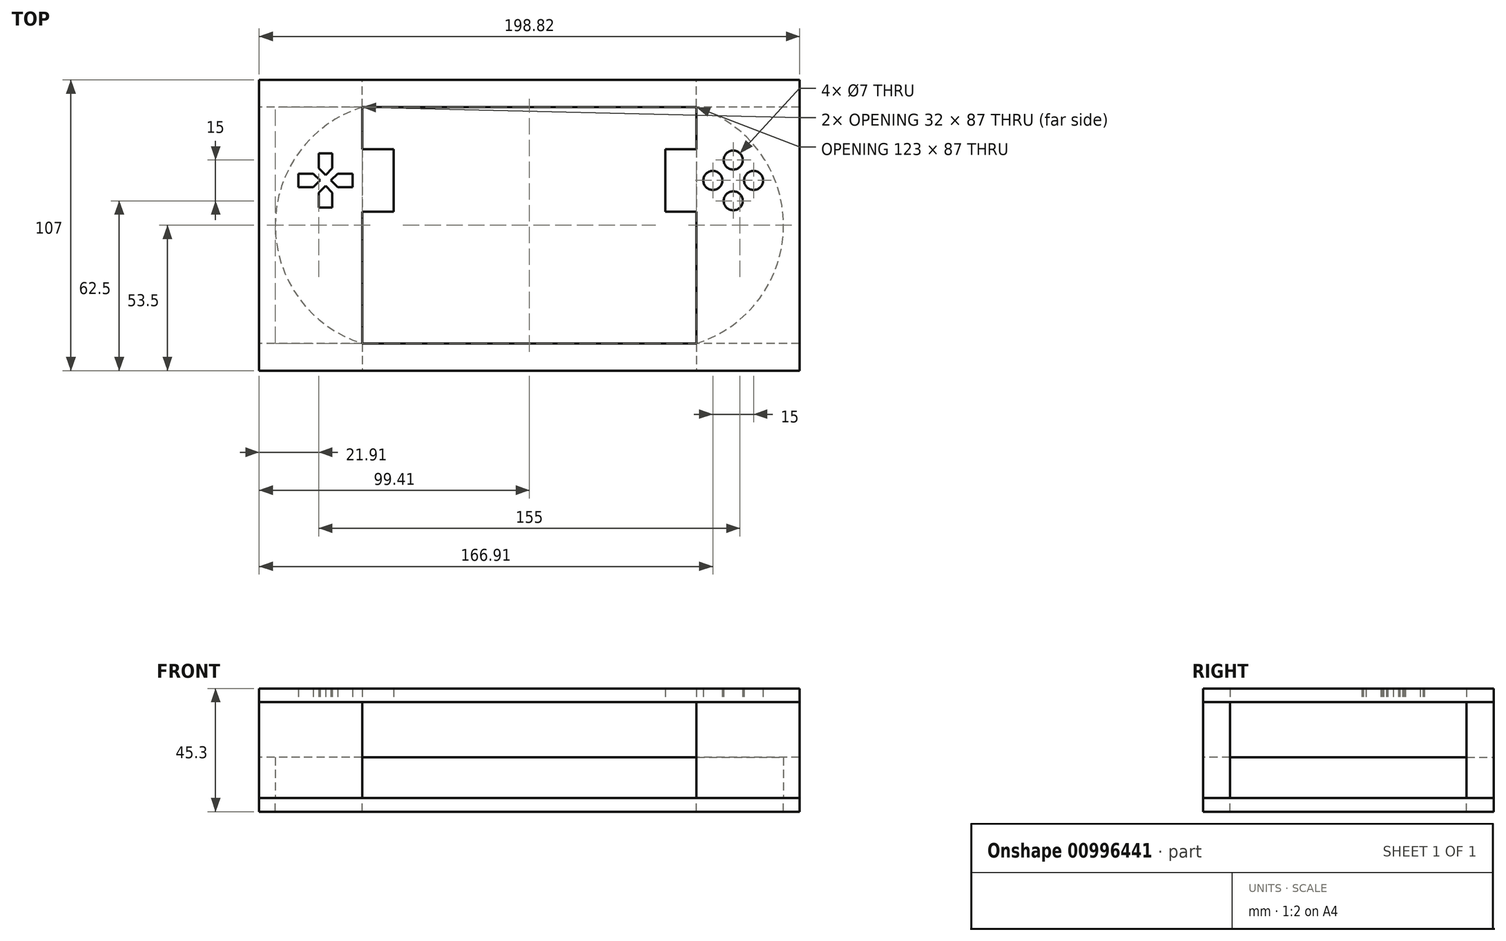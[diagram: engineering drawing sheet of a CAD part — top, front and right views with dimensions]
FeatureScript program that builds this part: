
annotation { "Feature Type Name" : "Feature", "Feature Type Description" : "" }
export const myFeature = defineFeature(function(context is Context, id is Id, definition is map)
    precondition{}
    {
        {
            var Q0;
            Q0=qCreatedBy(makeId("Top.planeOp"),FACE);
            var sketch = newSketch(context, id + "F0", { "sketchPlane" : qUnion([Q0])});
            skLineSegment(sketch, "E0.bottom", {"start": v(61.5, 43.5) * mm, "end": v(-61.5, 43.5) * mm});
            skLineSegment(sketch, "E0.top", {"start": v(61.5, -43.5) * mm, "end": v(-61.5, -43.5) * mm});
            skLineSegment(sketch, "E0.left", {"start": v(61.5, 43.5) * mm, "end": v(61.5, -43.5) * mm});
            skLineSegment(sketch, "E0.right", {"start": v(-61.5, 43.5) * mm, "end": v(-61.5, -43.5) * mm});
            skPoint(sketch, "E0.middle", {"position": v(0, 0) * mm});
            skArc(sketch, "E1", {"start": v(-61.5, 43.5) * mm, "mid": v(-93.5, 0) * mm, "end": v(-61.5, -43.5) * mm});
            skArc(sketch, "E2", {"start": v(61.5, -43.5) * mm, "mid": v(93.5, 0) * mm, "end": v(61.5, 43.5) * mm});
            skLineSegment(sketch, "E3.bottom", {"start": v(99.41, 43.5) * mm, "end": v(-99.41, 43.5) * mm});
            skLineSegment(sketch, "E3.top", {"start": v(99.41, -43.5) * mm, "end": v(-99.41, -43.5) * mm});
            skLineSegment(sketch, "E3.left", {"start": v(99.41, 43.5) * mm, "end": v(99.41, -43.5) * mm});
            skLineSegment(sketch, "E3.right", {"start": v(-99.41, 43.5) * mm, "end": v(-99.41, -43.5) * mm});
            skLineSegment(sketch, "E4.bottom", {"start": v(-99.41, 43.5) * mm, "end": v(99.41, 43.5) * mm});
            skLineSegment(sketch, "E4.top", {"start": v(-99.41, 43.5) * mm, "end": v(99.41, 43.5) * mm});
            skLineSegment(sketch, "E4.left", {"start": v(-99.41, 43.5) * mm, "end": v(-99.41, 43.5) * mm});
            skLineSegment(sketch, "E4.right", {"start": v(99.41, 43.5) * mm, "end": v(99.41, 43.5) * mm});
            skLineSegment(sketch, "E5.top", {"start": v(-99.41, 53.5) * mm, "end": v(99.41, 53.5) * mm});
            skLineSegment(sketch, "E5.left", {"start": v(-99.41, 43.5) * mm, "end": v(-99.41, 53.5) * mm});
            skLineSegment(sketch, "E5.right", {"start": v(99.41, 43.5) * mm, "end": v(99.41, 53.5) * mm});
            skLineSegment(sketch, "E6.bottom", {"start": v(-99.41, -43.5) * mm, "end": v(99.41, -43.5) * mm});
            skLineSegment(sketch, "E6.top", {"start": v(-99.41, -53.5) * mm, "end": v(99.41, -53.5) * mm});
            skLineSegment(sketch, "E6.left", {"start": v(-99.41, -43.5) * mm, "end": v(-99.41, -53.5) * mm});
            skLineSegment(sketch, "E6.right", {"start": v(99.41, -43.5) * mm, "end": v(99.41, -53.5) * mm});
            skLineSegment(sketch, "E7", {"start": v(-61.5, 43.5) * mm, "end": v(-61.5, 53.5) * mm});
            skLineSegment(sketch, "E8", {"start": v(61.5, 43.5) * mm, "end": v(61.5, 53.5) * mm});
            skLineSegment(sketch, "E9", {"start": v(61.5, -43.5) * mm, "end": v(61.5, -53.5) * mm});
            skLineSegment(sketch, "E10", {"start": v(-61.5, -43.5) * mm, "end": v(-61.5, -53.5) * mm});
            skSolve(sketch);
        }
        {
            var Q0;
            {var subQ2=sQuery(id+"F0.wireOp",EDGE,"E6.left");Q0=makeQuery(id+"F0.imprint","IMPRINT",FACE,{"disambiguationData":[TD([[makeQuery(id+"F0.imprint","IMPRINT",EDGE,{"derivedFrom":subQ2}),1.0]])]});}
            var Q1;
            {var subQ2=sQuery(id+"F0.wireOp",EDGE,"E5.left");Q1=makeQuery(id+"F0.imprint","IMPRINT",FACE,{"disambiguationData":[TD([[makeQuery(id+"F0.imprint","IMPRINT",EDGE,{"derivedFrom":subQ2}),-1.0]])]});}
            var Q2;
            {var subQ2=sQuery(id+"F0.wireOp",EDGE,"E5.right");Q2=makeQuery(id+"F0.imprint","IMPRINT",FACE,{"disambiguationData":[TD([[makeQuery(id+"F0.imprint","IMPRINT",EDGE,{"derivedFrom":subQ2}),1.0]])]});}
            var Q3;
            {var subQ2=sQuery(id+"F0.wireOp",EDGE,"E6.right");Q3=makeQuery(id+"F0.imprint","IMPRINT",FACE,{"disambiguationData":[TD([[makeQuery(id+"F0.imprint","IMPRINT",EDGE,{"derivedFrom":subQ2}),-1.0]])]});}
            extrude(context, id + "F1", {"entities" : qUnion([Q0, Q1, Q2, Q3]), "depth" : 35.3 * mm, "offsetDistance" : 25 * mm});
        }
        {
            var Q0;
            Q0=makeQuery(id+"F1.opExtrude","CAP_FACE",FACE,{"disambiguationData":[OSD([sQuery(id+"F0.wireOp",EDGE,"E6.bottom"),sQuery(id+"F0.wireOp",EDGE,"E6.top"),sQuery(id+"F0.wireOp",EDGE,"E6.left"),sQuery(id+"F0.wireOp",EDGE,"E10")])],"isStart":false});
            var sketch = newSketch(context, id + "F2", { "sketchPlane" : qUnion([Q0])});
            skLineSegment(sketch, "E11.bottom", {"start": v(61.5, 43.5) * mm, "end": v(-61.5, 43.5) * mm});
            skLineSegment(sketch, "E11.top", {"start": v(61.5, -43.5) * mm, "end": v(-61.5, -43.5) * mm});
            skLineSegment(sketch, "E11.left", {"start": v(61.5, 43.5) * mm, "end": v(61.5, -43.5) * mm});
            skLineSegment(sketch, "E11.right", {"start": v(-61.5, 43.5) * mm, "end": v(-61.5, -43.5) * mm});
            skPoint(sketch, "E11.middle", {"position": v(0, 0) * mm});
            skLineSegment(sketch, "E12.bottom", {"start": v(99.41, 43.5) * mm, "end": v(-99.41, 43.5) * mm});
            skLineSegment(sketch, "E12.top", {"start": v(99.41, -43.5) * mm, "end": v(-99.41, -43.5) * mm});
            skLineSegment(sketch, "E12.left", {"start": v(99.41, 43.5) * mm, "end": v(99.41, -43.5) * mm});
            skLineSegment(sketch, "E12.right", {"start": v(-99.41, 43.5) * mm, "end": v(-99.41, -43.5) * mm});
            skLineSegment(sketch, "E13.bottom", {"start": v(-99.41, 43.5) * mm, "end": v(99.41, 43.5) * mm});
            skLineSegment(sketch, "E13.top", {"start": v(-99.41, 43.5) * mm, "end": v(99.41, 43.5) * mm});
            skLineSegment(sketch, "E13.left", {"start": v(-99.41, 43.5) * mm, "end": v(-99.41, 43.5) * mm});
            skLineSegment(sketch, "E13.right", {"start": v(99.41, 43.5) * mm, "end": v(99.41, 43.5) * mm});
            skLineSegment(sketch, "E14.top", {"start": v(-99.41, 53.5) * mm, "end": v(99.41, 53.5) * mm});
            skLineSegment(sketch, "E14.left", {"start": v(-99.41, 43.5) * mm, "end": v(-99.41, 53.5) * mm});
            skLineSegment(sketch, "E14.right", {"start": v(99.41, 43.5) * mm, "end": v(99.41, 53.5) * mm});
            skLineSegment(sketch, "E15.bottom", {"start": v(-99.41, -43.5) * mm, "end": v(99.41, -43.5) * mm});
            skLineSegment(sketch, "E15.top", {"start": v(-99.41, -53.5) * mm, "end": v(99.41, -53.5) * mm});
            skLineSegment(sketch, "E15.left", {"start": v(-99.41, -43.5) * mm, "end": v(-99.41, -53.5) * mm});
            skLineSegment(sketch, "E15.right", {"start": v(99.41, -43.5) * mm, "end": v(99.41, -53.5) * mm});
            skPoint(sketch, "E16", {"position": v(-75, 16.5) * mm});
            skCircle(sketch, "E17", {"center": v(-75, 16.5) * mm, "radius": 11.5 * mm});
            skLineSegment(sketch, "E18.left", {"start": v(-85, 14) * mm, "end": v(-85, 19) * mm});
            skPoint(sketch, "E19.startSnap0", {"position": v(-85, 16.5) * mm});
            skPoint(sketch, "E20", {"position": v(-77, 16.5) * mm});
            skPoint(sketch, "E21", {"position": v(-79.5, 19) * mm});
            skPoint(sketch, "E22", {"position": v(-79.5, 14) * mm});
            skLineSegment(sketch, "E23", {"start": v(-79.5, 19) * mm, "end": v(-77, 16.5) * mm});
            skLineSegment(sketch, "E24", {"start": v(-79.5, 14) * mm, "end": v(-77, 16.5) * mm});
            skLineSegment(sketch, "E25", {"start": v(-85, 19) * mm, "end": v(-79.5, 19) * mm});
            skLineSegment(sketch, "E26", {"start": v(-85, 14) * mm, "end": v(-79.5, 14) * mm});
            skLineSegment(sketch, "E27.MirrorCS", {"start": v(-77.5, 21) * mm, "end": v(-75, 18.5) * mm});
            skLineSegment(sketch, "E28.MirrorCS", {"start": v(-72.5, 21) * mm, "end": v(-75, 18.5) * mm});
            skLineSegment(sketch, "E29", {"start": v(-77.5, 26.5) * mm, "end": v(-72.5, 26.5) * mm});
            skLineSegment(sketch, "E30", {"start": v(-77.5, 26.5) * mm, "end": v(-77.5, 21) * mm});
            skLineSegment(sketch, "E31", {"start": v(-72.5, 26.5) * mm, "end": v(-72.5, 21) * mm});
            skLineSegment(sketch, "E32.MirrorCS", {"start": v(-72.5, 12) * mm, "end": v(-75, 14.5) * mm});
            skLineSegment(sketch, "E33.MirrorCS", {"start": v(-77.5, 12) * mm, "end": v(-75, 14.5) * mm});
            skLineSegment(sketch, "E34.MirrorCS", {"start": v(-77.5, 6.5) * mm, "end": v(-77.5, 12) * mm});
            skLineSegment(sketch, "E35.MirrorCS", {"start": v(-77.5, 6.5) * mm, "end": v(-72.5, 6.5) * mm});
            skLineSegment(sketch, "E36.MirrorCS", {"start": v(-72.5, 6.5) * mm, "end": v(-72.5, 12) * mm});
            skLineSegment(sketch, "E37.MirrorCS", {"start": v(-70.5, 14) * mm, "end": v(-73, 16.5) * mm});
            skLineSegment(sketch, "E38.MirrorCS", {"start": v(-65, 14) * mm, "end": v(-70.5, 14) * mm});
            skLineSegment(sketch, "E39.MirrorCS", {"start": v(-65, 14) * mm, "end": v(-65, 19) * mm});
            skLineSegment(sketch, "E40.MirrorCS", {"start": v(-65, 19) * mm, "end": v(-70.5, 19) * mm});
            skCircle(sketch, "E41", {"center": v(75, 16.5) * mm, "radius": 11.5 * mm});
            skCircle(sketch, "E42", {"center": v(67.5, 16.5) * mm, "radius": 3.5 * mm});
            skCircle(sketch, "E43.1.0", {"center": v(75, 9) * mm, "radius": 3.5 * mm});
            skCircle(sketch, "E43.2.0", {"center": v(82.5, 16.5) * mm, "radius": 3.5 * mm});
            skCircle(sketch, "E43.3.0", {"center": v(75, 24) * mm, "radius": 3.5 * mm});
            skLineSegment(sketch, "E43.anchor1", {"start": v(75, 16.5) * mm, "end": v(67.5, 16.5) * mm, "construction": true});
            skLineSegment(sketch, "E43.anchor2", {"start": v(75, 16.5) * mm, "end": v(75, 24) * mm, "construction": true});
            skPoint(sketch, "E44", {"position": v(-55.75, 16.5) * mm});
            skLineSegment(sketch, "E45.bottom", {"start": v(-50, 5) * mm, "end": v(-61.5, 5) * mm});
            skLineSegment(sketch, "E45.top", {"start": v(-50, 28) * mm, "end": v(-61.5, 28) * mm});
            skLineSegment(sketch, "E45.left", {"start": v(-50, 5) * mm, "end": v(-50, 28) * mm});
            skLineSegment(sketch, "E45.right", {"start": v(-61.5, 5) * mm, "end": v(-61.5, 28) * mm});
            skLineSegment(sketch, "E46", {"start": v(-73, 16.5) * mm, "end": v(-70.5, 19) * mm});
            skPoint(sketch, "E47", {"position": v(55.75, 16.5) * mm});
            skLineSegment(sketch, "E48.bottom", {"start": v(61.5, 28) * mm, "end": v(50, 28) * mm});
            skLineSegment(sketch, "E48.top", {"start": v(61.5, 5) * mm, "end": v(50, 5) * mm});
            skLineSegment(sketch, "E48.left", {"start": v(61.5, 28) * mm, "end": v(61.5, 5) * mm});
            skLineSegment(sketch, "E48.right", {"start": v(50, 28) * mm, "end": v(50, 5) * mm});
            skSolve(sketch);
        }
        {
            var Q0;
            {var subQ0=sQuery(id+"F0.wireOp",EDGE,"E1");Q0=makeQuery(id+"F0.imprint","IMPRINT",FACE,{"disambiguationData":[TD([[makeQuery(id+"F0.imprint","IMPRINT",EDGE,{"derivedFrom":subQ0}),-1.0]])]});}
            var Q1;
            {var subQ2=sQuery(id+"F0.wireOp",EDGE,"E7");Q1=makeQuery(id+"F0.imprint","IMPRINT",FACE,{"disambiguationData":[TD([[makeQuery(id+"F0.imprint","IMPRINT",EDGE,{"derivedFrom":subQ2}),-1.0]])]});}
            var Q2;
            {var subQ0=sQuery(id+"F0.wireOp",EDGE,"E9");Q2=makeQuery(id+"F0.imprint","IMPRINT",FACE,{"disambiguationData":[TD([[makeQuery(id+"F0.imprint","IMPRINT",EDGE,{"derivedFrom":subQ0}),-1.0]])]});}
            var Q3;
            {var subQ0=sQuery(id+"F0.wireOp",EDGE,"E2");Q3=makeQuery(id+"F0.imprint","IMPRINT",FACE,{"disambiguationData":[TD([[makeQuery(id+"F0.imprint","IMPRINT",EDGE,{"derivedFrom":subQ0}),-1.0]])]});}
            extrude(context, id + "F3", {"entities" : qUnion([Q0, Q1, Q2, Q3]), "depth" : 15 * mm, "offsetDistance" : 25 * mm});
        }
        {
            var Q0;
            Q0 = qSketchRegion(id + "F2", true);
            var Q1;
            Q1=makeQuery(id+"F2.imprint","IMPRINT",FACE,{"disambiguationData":[TD([[makeQuery(id+"F2.imprint","IMPRINT",EDGE,{"derivedFrom":sQuery(id+"F2.wireOp",EDGE,"E17")}),1.0]])]});
            var Q2;
            Q2=makeQuery(id+"F2.imprint","IMPRINT",FACE,{"disambiguationData":[TD([[makeQuery(id+"F2.imprint","IMPRINT",EDGE,{"derivedFrom":sQuery(id+"F2.wireOp",EDGE,"E41")}),1.0]])]});
            var Q3;
            Q3=makeQuery(id+"F2.imprint","IMPRINT",FACE,{"disambiguationData":[TD([[makeQuery(id+"F2.imprint","IMPRINT",EDGE,{"derivedFrom":sQuery(id+"F2.wireOp",EDGE,"E45.bottom")}),-1.0]])]});
            var Q4;
            Q4=makeQuery(id+"F2.imprint","IMPRINT",FACE,{"disambiguationData":[TD([[makeQuery(id+"F2.imprint","IMPRINT",EDGE,{"derivedFrom":sQuery(id+"F2.wireOp",EDGE,"E48.bottom")}),1.0]])]});
            extrude(context, id + "F4", {"entities" : qUnion([Q0, Q1, Q2, Q3, Q4]), "depth" : 5 * mm, "offsetDistance" : 25 * mm});
        }
        {
            var Q0;
            Q0 = qSketchRegion(id + "F0", true);
            var Q1;
            {var subQ0=sQuery(id+"F0.wireOp",EDGE,"E0.left");Q1=makeQuery(id+"F0.imprint","IMPRINT",FACE,{"disambiguationData":[TD([[makeQuery(id+"F0.imprint","IMPRINT",EDGE,{"derivedFrom":subQ0}),-1.0]])]});}
            extrude(context, id + "F5", {"entities" : qUnion([Q0, Q1]), "oppositeDirection" : true, "depth" : 5 * mm, "offsetDistance" : 25 * mm});
        }
    });
